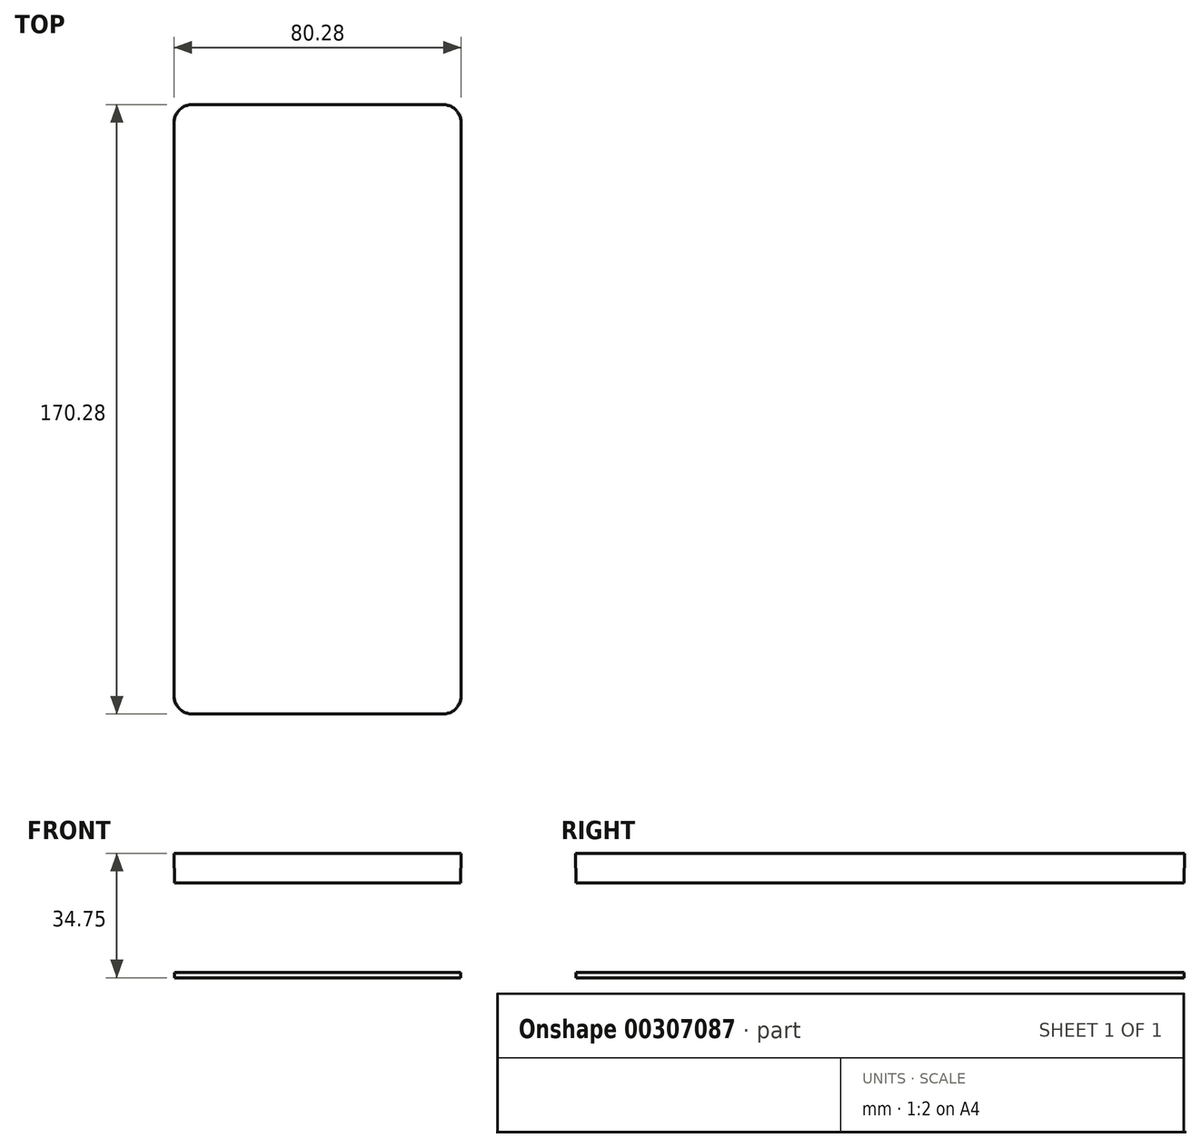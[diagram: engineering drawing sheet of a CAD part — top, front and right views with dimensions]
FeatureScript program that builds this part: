
annotation { "Feature Type Name" : "Feature", "Feature Type Description" : "" }
export const myFeature = defineFeature(function(context is Context, id is Id, definition is map)
    precondition{}
    {
        {
            var Q0;
            Q0=qCreatedBy(makeId("Top.planeOp"),FACE);
            var sketch = newSketch(context, id + "F0", { "sketchPlane" : qUnion([Q0])});
            skLineSegment(sketch, "E0.bottom", {"start": v(40, 85) * mm, "end": v(-40, 85) * mm});
            skLineSegment(sketch, "E0.top", {"start": v(40, -85) * mm, "end": v(-40, -85) * mm});
            skLineSegment(sketch, "E0.left", {"start": v(40, 85) * mm, "end": v(40, -85) * mm});
            skLineSegment(sketch, "E0.right", {"start": v(-40, 85) * mm, "end": v(-40, -85) * mm});
            skPoint(sketch, "E0.middle", {"position": v(0, 0) * mm});
            skSolve(sketch);
        }
        {
            var Q0;
            Q0 = qSketchRegion(id + "F0", true);
            extrude(context, id + "F1", {"entities" : qUnion([Q0]), "depth" : 8.25 * mm, "hasDraft" : true, "draftAngle" : 1 * degree});
        }
        {
            var Q0;
            Q0=makeQuery(id+"F1.opExtrude","SWEPT_EDGE",EDGE,{"disambiguationData":[OSD([sQuery(id+"F0.wireOp",EDGE,"E0.top"),sQuery(id+"F0.wireOp",EDGE,"E0.right")])]});
            var Q1;
            Q1=makeQuery(id+"F1.opExtrude","SWEPT_EDGE",EDGE,{"disambiguationData":[OSD([sQuery(id+"F0.wireOp",EDGE,"E0.top"),sQuery(id+"F0.wireOp",EDGE,"E0.left")])]});
            var Q2;
            Q2=makeQuery(id+"F1.opExtrude","SWEPT_EDGE",EDGE,{"disambiguationData":[OSD([sQuery(id+"F0.wireOp",EDGE,"E0.bottom"),sQuery(id+"F0.wireOp",EDGE,"E0.right")])]});
            var Q3;
            Q3=makeQuery(id+"F1.opExtrude","SWEPT_EDGE",EDGE,{"disambiguationData":[OSD([sQuery(id+"F0.wireOp",EDGE,"E0.bottom"),sQuery(id+"F0.wireOp",EDGE,"E0.left")])]});
            fillet(context, id + "F2", {"entities" : qUnion([Q0, Q1, Q2, Q3]), "radius" : 5 * mm, "tangentPropagation" : true, "allowEdgeOverflow" : false});
        }
        {
            var Q0;
            Q0=makeQuery(id+"F1.opExtrude","CAP_FACE",FACE,{"disambiguationData":[OSD([sQuery(id+"F0.wireOp",EDGE,"E0.bottom"),sQuery(id+"F0.wireOp",EDGE,"E0.top"),sQuery(id+"F0.wireOp",EDGE,"E0.left"),sQuery(id+"F0.wireOp",EDGE,"E0.right")])],"isStart":true});
            cPlane(context, id + "F3", {"entities" : qUnion([Q0]), "cplaneType" : CPlaneType.OFFSET, "offset" : 25 * mm, "width" : 150 * mm, "height" : 150 * mm});
        }
        {
            var Q0;
            Q0=qCreatedBy(id+"F3.planeOp",FACE);
            var sketch = newSketch(context, id + "F4", { "sketchPlane" : qUnion([Q0])});
            skLineSegment(sketch, "E1.0.0", {"start": v(40, -80) * mm, "end": v(40, 80) * mm});
            skEllipticalArc(sketch, "E1.0.1", {});
            skLineSegment(sketch, "E1.0.2", {"start": v(35, 85) * mm, "end": v(-35, 85) * mm});
            skEllipticalArc(sketch, "E1.0.3", {});
            skLineSegment(sketch, "E1.0.4", {"start": v(-40, -80) * mm, "end": v(-40, 80) * mm});
            skEllipticalArc(sketch, "E1.0.5", {});
            skLineSegment(sketch, "E1.0.6", {"start": v(35, -85) * mm, "end": v(-35, -85) * mm});
            skEllipticalArc(sketch, "E1.0.7", {});
            const initialGuessF4  = {"E1.0.1": [0.03499923835978046, 0.0799992383597805, -0.7071067811865476, -0.7071067811865476, 0.005001523164455246, 0.005, 2.356346783439925, 3.9268385237396597], "E1.0.3": [-0.03499923835978047, 0.07999923835978047, 0.7071067811865476, -0.7071067811865476, 0.005001523164455246, 0.005, 2.356346783439925, 3.926838523739661], "E1.0.5": [-0.03499923835978047, -0.07999923835978046, 0.7071067811865476, 0.7071067811865476, 0.005001523164455246, 0.005, 2.356346783439928, 3.926838523739661], "E1.0.7": [0.034999238359780464, -0.07999923835978047, -0.7071067811865476, 0.7071067811865476, 0.005001523164455246, 0.005, 2.356346783439925, 3.9268385237396584]};
            skSetInitialGuess(sketch, initialGuessF4);
            skSolve(sketch);
        }
        {
            var Q0;
            Q0 = qSketchRegion(id + "F4", true);
            extrude(context, id + "F5", {"entities" : qUnion([Q0]), "depth" : 1.5 * mm});
        }
    });
